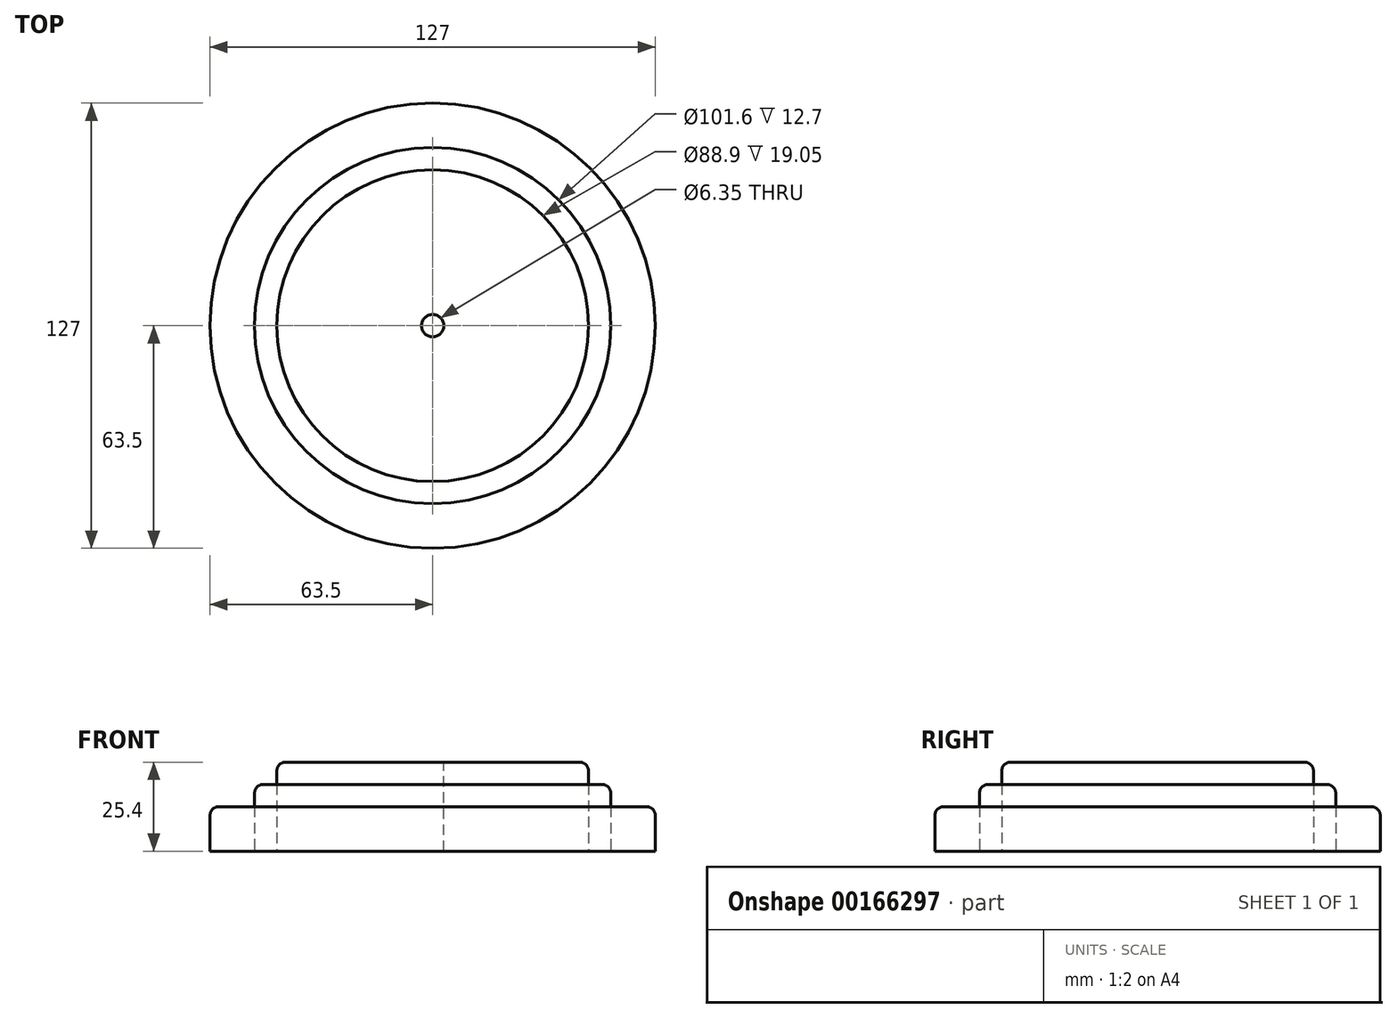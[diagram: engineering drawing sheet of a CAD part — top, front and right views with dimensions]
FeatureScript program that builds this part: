
annotation { "Feature Type Name" : "Feature", "Feature Type Description" : "" }
export const myFeature = defineFeature(function(context is Context, id is Id, definition is map)
    precondition{}
    {
        {
            var Q0;
            Q0=qCreatedBy(makeId("Top.planeOp"),FACE);
            var sketch = newSketch(context, id + "F0", { "sketchPlane" : qUnion([Q0])});
            skCircle(sketch, "E0", {"center": v(0, 0) * mm, "radius": 63.5 * mm});
            skCircle(sketch, "E1", {"center": v(0, 0) * mm, "radius": 50.8 * mm});
            skCircle(sketch, "E2", {"center": v(0, 0) * mm, "radius": 44.45 * mm});
            skSolve(sketch);
        }
        {
            var Q0;
            Q0=makeQuery(id+"F0.imprint","IMPRINT",FACE,{"disambiguationData":[TD([[makeQuery(id+"F0.imprint","IMPRINT",EDGE,{"derivedFrom":sQuery(id+"F0.wireOp",EDGE,"E2")}),1.0]])]});
            extrude(context, id + "F1", {"entities" : qUnion([Q0]), "depth" : 25.4 * mm});
        }
        {
            var Q0;
            Q0 = qSketchRegion(id + "F0", true);
            extrude(context, id + "F2", {"entities" : qUnion([Q0]), "depth" : 12.7 * mm});
        }
        {
            var Q0;
            Q0=makeQuery(id+"F0.imprint","IMPRINT",FACE,{"disambiguationData":[TD([[makeQuery(id+"F0.imprint","IMPRINT",EDGE,{"derivedFrom":sQuery(id+"F0.wireOp",EDGE,"E1")}),1.0]])]});
            extrude(context, id + "F3", {"entities" : qUnion([Q0]), "depth" : 19.05 * mm});
        }
        {
            var Q0;
            Q0=makeQuery(id+"F1.opExtrude","CAP_FACE",FACE,{"disambiguationData":[OSD([sQuery(id+"F0.wireOp",EDGE,"E2")])],"isStart":false});
            var sketch = newSketch(context, id + "F4", { "sketchPlane" : qUnion([Q0])});
            skPoint(sketch, "E3", {"position": v(0, 0) * mm});
            skSolve(sketch);
        }
        {
            var Q0;
            Q0=sQuery(id+"F4.wireOp",VERTEX,"E3");
            var Q1;
            Q1=makeQuery(id+"F1.opExtrude","SWEPT_BODY",BODY,{"disambiguationData":[OSD([sQuery(id+"F0.wireOp",EDGE,"E2")])]});
            hole(context, id + "F5", {"style" : HoleStyle.SIMPLE, "endStyle" : HoleEndStyle.THROUGH, "holeDiameter" : 6.35 * mm, "locations" : qUnion([Q0]), "scope" : qUnion([Q1]), "isTappedThrough" : true});
        }
        {
            var Q0;
            Q0=makeQuery(id+"F1.opExtrude","CAP_EDGE",EDGE,{"disambiguationData":[OSD([sQuery(id+"F0.wireOp",EDGE,"E2")])],"isStart":false});
            var Q1;
            Q1=makeQuery(id+"F3.opExtrude","CAP_EDGE",EDGE,{"disambiguationData":[OSD([sQuery(id+"F0.wireOp",EDGE,"E1")])],"isStart":false});
            var Q2;
            Q2=makeQuery(id+"F2.opExtrude","CAP_EDGE",EDGE,{"disambiguationData":[OSD([sQuery(id+"F0.wireOp",EDGE,"E0")])],"isStart":false});
            fillet(context, id + "F6", {"entities" : qUnion([Q0, Q1, Q2]), "radius" : 2.54 * mm, "tangentPropagation" : true, "allowEdgeOverflow" : false});
        }
    });
